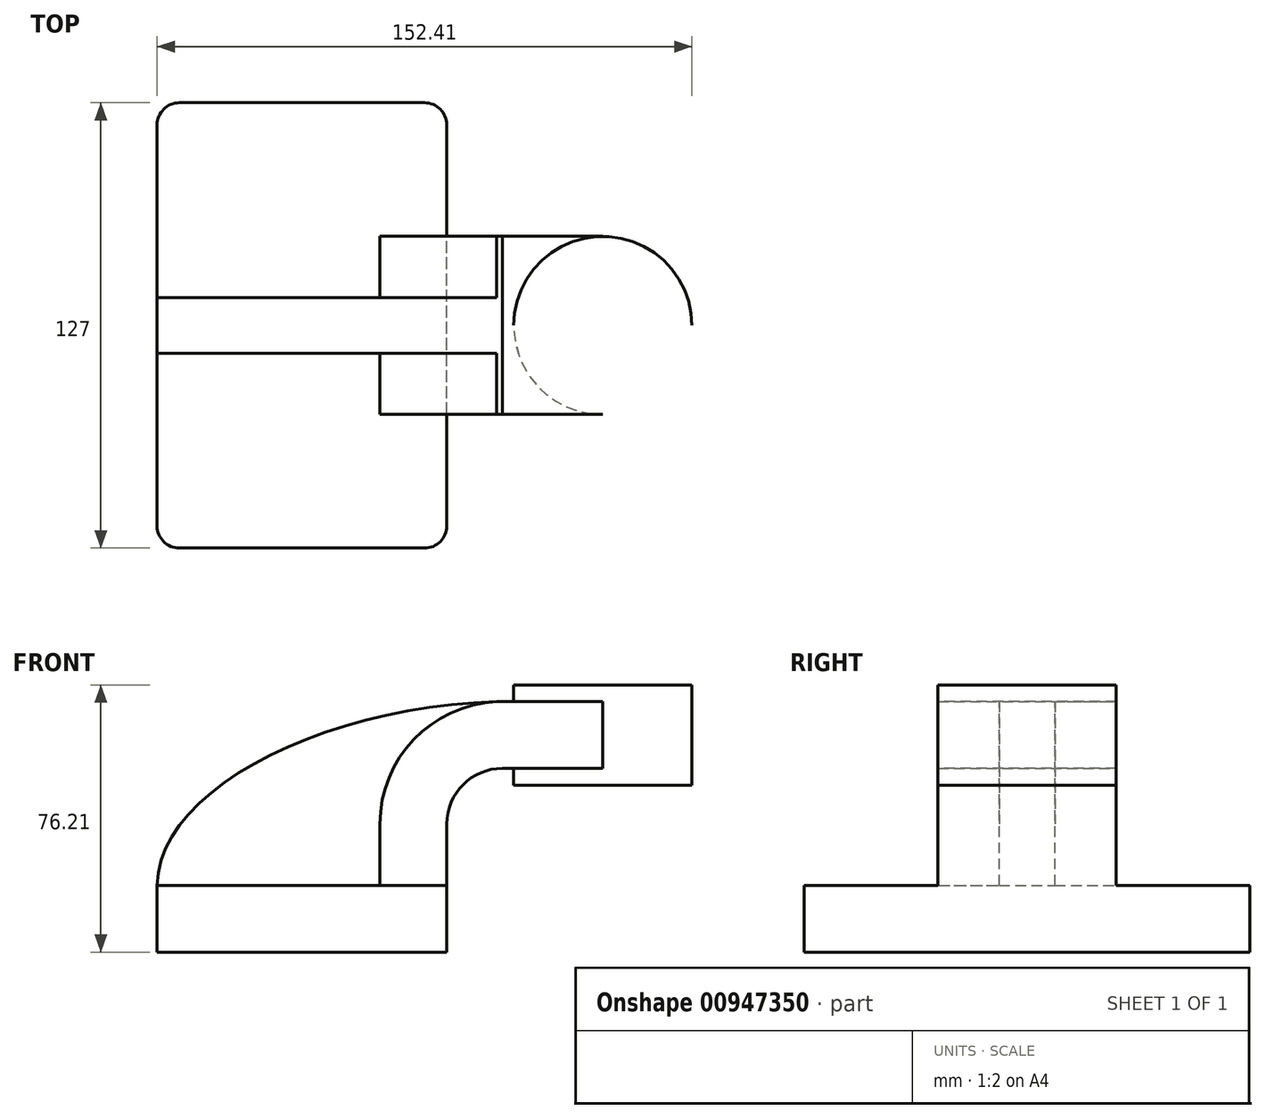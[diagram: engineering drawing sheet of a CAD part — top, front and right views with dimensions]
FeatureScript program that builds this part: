
annotation { "Feature Type Name" : "Feature", "Feature Type Description" : "" }
export const myFeature = defineFeature(function(context is Context, id is Id, definition is map)
    precondition{}
    {
        {
            var Q0;
            Q0=qCreatedBy(makeId("Front.planeOp"),FACE);
            var sketch = newSketch(context, id + "F0", { "sketchPlane" : qUnion([Q0])});
            skLineSegment(sketch, "E0.bottom", {"start": v(-41.28, 9.52) * mm, "end": v(41.28, 9.53) * mm});
            skLineSegment(sketch, "E0.top", {"start": v(-41.28, -9.53) * mm, "end": v(41.28, -9.53) * mm});
            skLineSegment(sketch, "E0.left", {"start": v(-41.28, 9.52) * mm, "end": v(-41.28, -9.53) * mm});
            skLineSegment(sketch, "E0.right", {"start": v(41.28, 9.53) * mm, "end": v(41.28, -9.52) * mm});
            skPoint(sketch, "E0.middle", {"position": v(0, 0) * mm});
            skLineSegment(sketch, "E1.bottom", {"start": v(60.32, 38.1) * mm, "end": v(111.12, 38.1) * mm});
            skLineSegment(sketch, "E1.top", {"start": v(60.32, 66.67) * mm, "end": v(111.12, 66.67) * mm});
            skLineSegment(sketch, "E1.left", {"start": v(60.32, 38.1) * mm, "end": v(60.32, 66.67) * mm});
            skLineSegment(sketch, "E1.right", {"start": v(111.12, 38.1) * mm, "end": v(111.12, 66.67) * mm});
            skPoint(sketch, "E1.middle", {"position": v(85.72, 52.39) * mm});
            skLineSegment(sketch, "E2", {"start": v(41.28, 9.53) * mm, "end": v(41.28, 27) * mm});
            skArc(sketch, "E3", {"start": v(41.27, 27) * mm, "mid": v(45.92, 38.23) * mm, "end": v(57.15, 42.88) * mm});
            skLineSegment(sketch, "E4", {"start": v(57.15, 42.88) * mm, "end": v(85.72, 42.88) * mm});
            skLineSegment(sketch, "E5.0", {"start": v(57.15, 61.93) * mm, "end": v(85.72, 61.93) * mm});
            skArc(sketch, "E5.1", {"start": v(22.22, 27) * mm, "mid": v(32.45, 51.7) * mm, "end": v(57.15, 61.93) * mm});
            skLineSegment(sketch, "E5.2", {"start": v(22.22, 9.53) * mm, "end": v(22.22, 27) * mm});
            skFitSpline(sketch, "E6", {"points": [v(-41.28, 9.52) * mm, v(57.15, 61.93) * mm], "startDerivative": vector(1, 83.12) * mm, "endDerivative": vector(150.3, 2.84) * mm});
            skLineSegment(sketch, "E7", {"start": v(85.72, 61.93) * mm, "end": v(85.72, 42.88) * mm});
            skLineSegment(sketch, "E8", {"start": v(85.72, 66.67) * mm, "end": v(85.73, 38.1) * mm});
            skSolve(sketch);
        }
        {
            var Q0;
            Q0=makeQuery(id+"F0.imprint","IMPRINT",FACE,{"disambiguationData":[TD([[makeQuery(id+"F0.imprint","IMPRINT",EDGE,{"derivedFrom":sQuery(id+"F0.wireOp",EDGE,"E0.top")}),1.0]])]});
            extrude(context, id + "F1", {"entities" : qUnion([Q0]), "endBound" : BoundingType.SYMMETRIC, "depth" : 127 * mm, "offsetDistance" : 25.4 * mm});
        }
        {
            var Q0;
            {var subQ1=sQuery(id+"F0.wireOp",EDGE,"E2");Q0=makeQuery(id+"F0.imprint","IMPRINT",FACE,{"disambiguationData":[TD([[makeQuery(id+"F0.imprint","IMPRINT",EDGE,{"derivedFrom":subQ1}),1.0]])]});}
            var Q1;
            {var subQ5=sQuery(id+"F0.wireOp",EDGE,"E7");Q1=makeQuery(id+"F0.imprint","IMPRINT",FACE,{"disambiguationData":[TD([[makeQuery(id+"F0.imprint","IMPRINT",EDGE,{"derivedFrom":subQ5}),-1.0]])]});}
            extrude(context, id + "F2", {"entities" : qUnion([Q0, Q1]), "operationType" : NewBodyOperationType.ADD, "endBound" : BoundingType.SYMMETRIC, "depth" : 50.8 * mm, "offsetDistance" : 25.4 * mm});
        }
        {
            var Q0;
            {var subQ3=sQuery(id+"F0.wireOp",EDGE,"E5.2");Q0=makeQuery(id+"F0.imprint","IMPRINT",FACE,{"disambiguationData":[TD([[makeQuery(id+"F0.imprint","IMPRINT",EDGE,{"derivedFrom":subQ3}),1.0]])]});}
            extrude(context, id + "F3", {"entities" : qUnion([Q0]), "operationType" : NewBodyOperationType.ADD, "endBound" : BoundingType.SYMMETRIC, "depth" : 15.88 * mm, "offsetDistance" : 25.4 * mm});
        }
        {
            var Q0;
            {var subQ0=sQuery(id+"F0.wireOp",EDGE,"E1.right");Q0=makeQuery(id+"F0.imprint","IMPRINT",FACE,{"disambiguationData":[TD([[makeQuery(id+"F0.imprint","IMPRINT",EDGE,{"derivedFrom":subQ0}),1.0]])]});}
            var Q1;
            Q1=sQuery(id+"F0.wireOp",EDGE,"E8");
            revolve(context, id + "F4", {"operationType" : NewBodyOperationType.ADD, "surfaceOperationType" : NewSurfaceOperationType.NEW, "entities" : qUnion([Q0]), "axis" : qUnion([Q1]), "revolveType" : RevolveType.FULL});
        }
        {
            var Q0;
            Q0=makeQuery(id+"F1.opExtrude","CAP_EDGE",EDGE,{"disambiguationData":[OSD([sQuery(id+"F0.wireOp",EDGE,"E0.left")])],"isStart":false});
            var Q1;
            Q1=makeQuery(id+"F1.opExtrude","CAP_EDGE",EDGE,{"disambiguationData":[OSD([sQuery(id+"F0.wireOp",EDGE,"E0.right")])],"isStart":false});
            var Q2;
            Q2=makeQuery(id+"F1.opExtrude","CAP_EDGE",EDGE,{"disambiguationData":[OSD([sQuery(id+"F0.wireOp",EDGE,"E0.right")])],"isStart":true});
            var Q3;
            Q3=makeQuery(id+"F1.opExtrude","CAP_EDGE",EDGE,{"disambiguationData":[OSD([sQuery(id+"F0.wireOp",EDGE,"E0.left")])],"isStart":true});
            fillet(context, id + "F5", {"entities" : qUnion([Q0, Q1, Q2, Q3]), "radius" : 6.35 * mm, "tangentPropagation" : true, "allowEdgeOverflow" : false});
        }
    });
